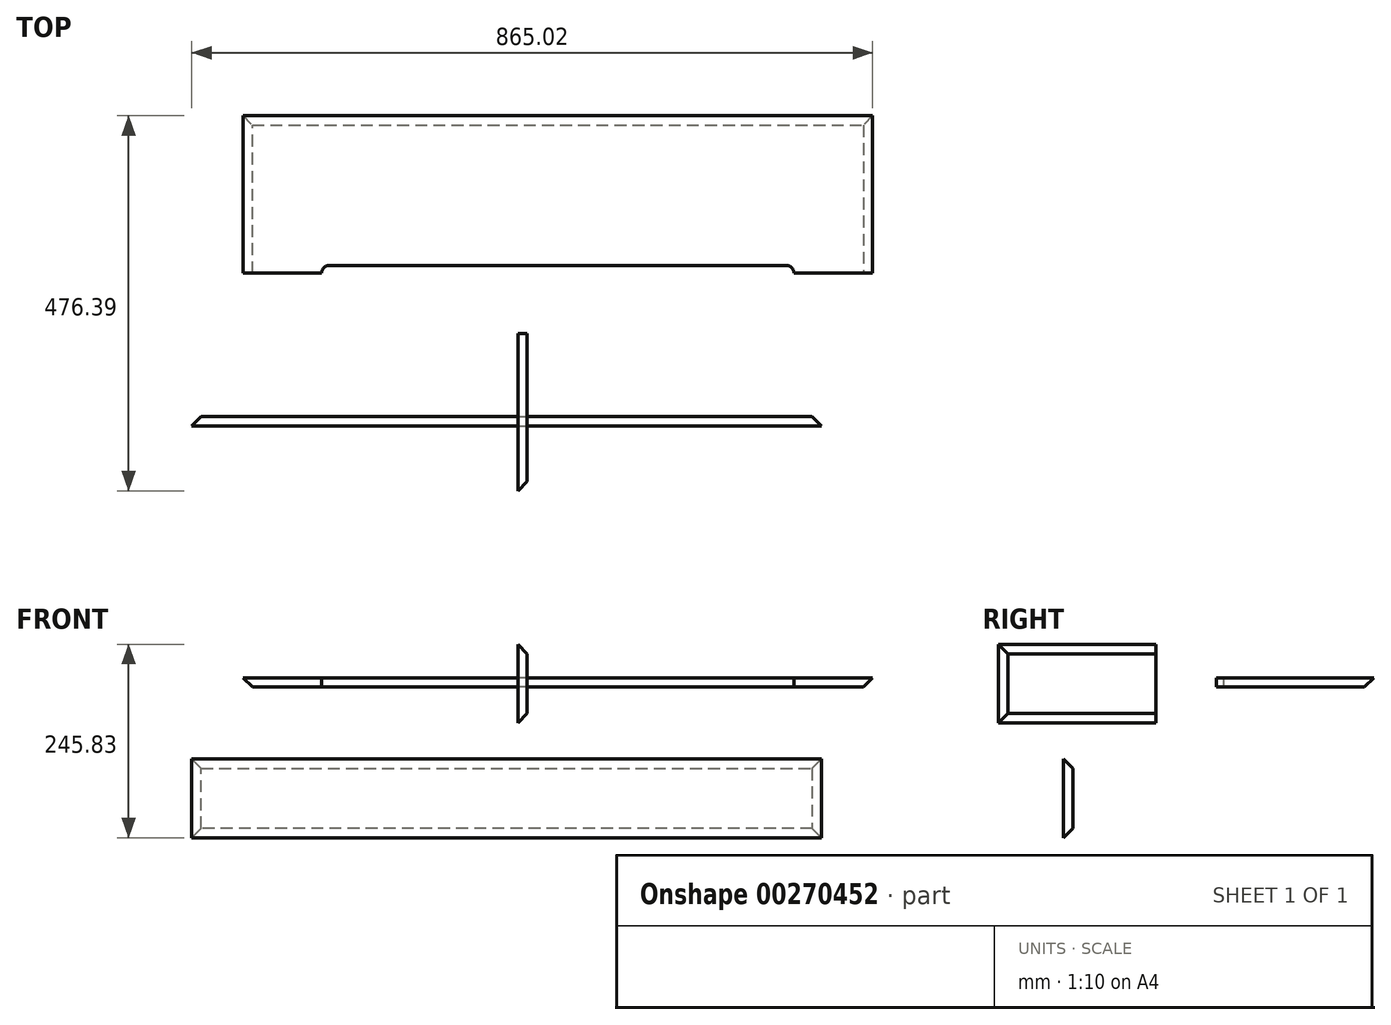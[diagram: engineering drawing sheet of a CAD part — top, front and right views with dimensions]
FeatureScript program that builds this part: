
annotation { "Feature Type Name" : "Feature", "Feature Type Description" : "" }
export const myFeature = defineFeature(function(context is Context, id is Id, definition is map)
    precondition{}
    {
        {
            var Q0;
            Q0=qCreatedBy(makeId("Front.planeOp"),FACE);
            var sketch = newSketch(context, id + "F0", { "sketchPlane" : qUnion([Q0])});
            skLineSegment(sketch, "E0.bottom", {"start": v(-414.23, -91.31) * mm, "end": v(385.77, -91.31) * mm});
            skLineSegment(sketch, "E0.top", {"start": v(-414.23, -191.31) * mm, "end": v(385.77, -191.31) * mm});
            skLineSegment(sketch, "E0.left", {"start": v(-414.23, -91.31) * mm, "end": v(-414.23, -191.31) * mm});
            skLineSegment(sketch, "E0.right", {"start": v(385.77, -91.31) * mm, "end": v(385.77, -191.31) * mm});
            skSolve(sketch);
        }
        {
            var Q0;
            Q0 = qSketchRegion(id + "F0", true);
            extrude(context, id + "F1", {"entities" : qUnion([Q0]), "depth" : 12 * mm});
        }
        {
            var Q0;
            Q0=qCreatedBy(makeId("Right.planeOp"),FACE);
            var sketch = newSketch(context, id + "F2", { "sketchPlane" : qUnion([Q0])});
            skLineSegment(sketch, "E1.bottom", {"start": v(105.79, 54.52) * mm, "end": v(-94.21, 54.52) * mm});
            skLineSegment(sketch, "E1.top", {"start": v(105.79, -45.48) * mm, "end": v(-94.21, -45.48) * mm});
            skLineSegment(sketch, "E1.left", {"start": v(105.79, 54.52) * mm, "end": v(105.79, -45.48) * mm});
            skLineSegment(sketch, "E1.right", {"start": v(-94.21, 54.52) * mm, "end": v(-94.21, -45.48) * mm});
            skSolve(sketch);
        }
        {
            var Q0;
            Q0 = qSketchRegion(id + "F2", true);
            extrude(context, id + "F3", {"entities" : qUnion([Q0]), "depth" : 12 * mm});
        }
        {
            var Q0;
            Q0=makeQuery(id+"F3.opExtrude","CAP_EDGE",EDGE,{"disambiguationData":[OSD([sQuery(id+"F2.wireOp",EDGE,"E1.right")])],"isStart":false});
            chamfer(context, id + "F4", {"entities" : qUnion([Q0]), "width" : 12 * mm, "tangentPropagation" : true});
        }
        {
            var Q0;
            Q0=makeQuery(id+"F1.opExtrude","CAP_EDGE",EDGE,{"disambiguationData":[OSD([sQuery(id+"F0.wireOp",EDGE,"E0.left")])],"isStart":true});
            chamfer(context, id + "F5", {"entities" : qUnion([Q0]), "width" : 12 * mm, "tangentPropagation" : true});
        }
        {
            var Q0;
            Q0=makeQuery(id+"F1.opExtrude","CAP_EDGE",EDGE,{"disambiguationData":[OSD([sQuery(id+"F0.wireOp",EDGE,"E0.right")])],"isStart":true});
            chamfer(context, id + "F6", {"entities" : qUnion([Q0]), "width" : 12 * mm, "tangentPropagation" : true});
        }
        {
            var Q0;
            Q0=qCreatedBy(makeId("Top.planeOp"),FACE);
            var sketch = newSketch(context, id + "F7", { "sketchPlane" : qUnion([Q0])});
            skLineSegment(sketch, "E2.bottom", {"start": v(-349.21, 382.18) * mm, "end": v(450.79, 382.18) * mm});
            skLineSegment(sketch, "E2.top", {"start": v(-349.21, 182.18) * mm, "end": v(450.79, 182.18) * mm});
            skLineSegment(sketch, "E2.left", {"start": v(-349.21, 382.18) * mm, "end": v(-349.21, 182.18) * mm});
            skLineSegment(sketch, "E2.right", {"start": v(450.79, 382.18) * mm, "end": v(450.79, 182.18) * mm});
            skSolve(sketch);
        }
        {
            var Q0;
            Q0=makeQuery(id+"F7.imprint","IMPRINT",FACE,{"disambiguationData":[TD([[makeQuery(id+"F7.imprint","IMPRINT",EDGE,{"derivedFrom":sQuery(id+"F7.wireOp",EDGE,"E2.bottom")}),-1.0]])]});
            extrude(context, id + "F8", {"entities" : qUnion([Q0]), "depth" : 12 * mm});
        }
        {
            var Q0;
            Q0=makeQuery(id+"F1.opExtrude","CAP_EDGE",EDGE,{"disambiguationData":[OSD([sQuery(id+"F0.wireOp",EDGE,"E0.bottom")])],"isStart":true});
            chamfer(context, id + "F9", {"entities" : qUnion([Q0]), "width" : 12 * mm, "tangentPropagation" : true});
        }
        {
            var Q0;
            Q0=makeQuery(id+"F1.opExtrude","CAP_EDGE",EDGE,{"disambiguationData":[OSD([sQuery(id+"F0.wireOp",EDGE,"E0.top")])],"isStart":true});
            chamfer(context, id + "F10", {"entities" : qUnion([Q0]), "width" : 12 * mm, "tangentPropagation" : true});
        }
        {
            var Q0;
            Q0=makeQuery(id+"F8.opExtrude","CAP_EDGE",EDGE,{"disambiguationData":[OSD([sQuery(id+"F7.wireOp",EDGE,"E2.bottom")])],"isStart":true});
            chamfer(context, id + "F11", {"entities" : qUnion([Q0]), "width" : 12 * mm, "tangentPropagation" : true});
        }
        {
            var Q0;
            Q0=makeQuery(id+"F8.opExtrude","CAP_EDGE",EDGE,{"disambiguationData":[OSD([sQuery(id+"F7.wireOp",EDGE,"E2.left")])],"isStart":true});
            chamfer(context, id + "F12", {"entities" : qUnion([Q0]), "width" : 12 * mm, "tangentPropagation" : true});
        }
        {
            var Q0;
            Q0=makeQuery(id+"F8.opExtrude","CAP_EDGE",EDGE,{"disambiguationData":[OSD([sQuery(id+"F7.wireOp",EDGE,"E2.right")])],"isStart":true});
            chamfer(context, id + "F13", {"entities" : qUnion([Q0]), "width" : 12 * mm, "tangentPropagation" : true});
        }
        {
            var Q0;
            Q0=makeQuery(id+"F3.opExtrude","CAP_EDGE",EDGE,{"disambiguationData":[OSD([sQuery(id+"F2.wireOp",EDGE,"E1.bottom")])],"isStart":false});
            chamfer(context, id + "F14", {"entities" : qUnion([Q0]), "width" : 12 * mm, "tangentPropagation" : true});
        }
        {
            var Q0;
            Q0=makeQuery(id+"F3.opExtrude","CAP_EDGE",EDGE,{"disambiguationData":[OSD([sQuery(id+"F2.wireOp",EDGE,"E1.top")])],"isStart":false});
            chamfer(context, id + "F15", {"entities" : qUnion([Q0]), "width" : 12 * mm, "tangentPropagation" : true});
        }
        {
            var Q0;
            Q0=makeQuery(id+"F8.opExtrude","CAP_FACE",FACE,{"disambiguationData":[OSD([sQuery(id+"F7.wireOp",EDGE,"E2.bottom"),sQuery(id+"F7.wireOp",EDGE,"E2.top"),sQuery(id+"F7.wireOp",EDGE,"E2.left"),sQuery(id+"F7.wireOp",EDGE,"E2.right")])],"isStart":false});
            var sketch = newSketch(context, id + "F16", { "sketchPlane" : qUnion([Q0])});
            skLineSegment(sketch, "E3.bottom", {"start": v(350.79, 192.18) * mm, "end": v(-249.21, 192.18) * mm});
            skLineSegment(sketch, "E3.top", {"start": v(350.79, 172.18) * mm, "end": v(-249.21, 172.18) * mm});
            skLineSegment(sketch, "E3.left", {"start": v(350.79, 192.18) * mm, "end": v(350.79, 172.18) * mm});
            skLineSegment(sketch, "E3.right", {"start": v(-249.21, 192.18) * mm, "end": v(-249.21, 172.18) * mm});
            skPoint(sketch, "E3.middle", {"position": v(50.79, 182.18) * mm});
            skSolve(sketch);
        }
        {
            var Q0;
            Q0 = qSketchRegion(id + "F16", true);
            extrude(context, id + "F17", {"entities" : qUnion([Q0]), "operationType" : NewBodyOperationType.REMOVE, "oppositeDirection" : true, "depth" : 25 * mm});
        }
        {
            var Q0;
            Q0=makeQuery(id+"F17.boolean.opBoolean","COPY",EDGE,{"derivedFrom":makeQuery(id+"F17.opExtrude","SWEPT_EDGE",EDGE,{"disambiguationData":[OSD([sQuery(id+"F16.wireOp",EDGE,"E3.bottom"),sQuery(id+"F16.wireOp",EDGE,"E3.right")])]})});
            fillet(context, id + "F18", {"entities" : qUnion([Q0]), "radius" : 10 * mm, "tangentPropagation" : true, "allowEdgeOverflow" : false});
        }
        {
            var Q0;
            Q0=makeQuery(id+"F17.boolean.opBoolean","COPY",EDGE,{"derivedFrom":makeQuery(id+"F17.opExtrude","SWEPT_EDGE",EDGE,{"disambiguationData":[OSD([sQuery(id+"F16.wireOp",EDGE,"E3.bottom"),sQuery(id+"F16.wireOp",EDGE,"E3.left")])]})});
            fillet(context, id + "F19", {"entities" : qUnion([Q0]), "radius" : 10 * mm, "tangentPropagation" : true, "allowEdgeOverflow" : false});
        }
    });
